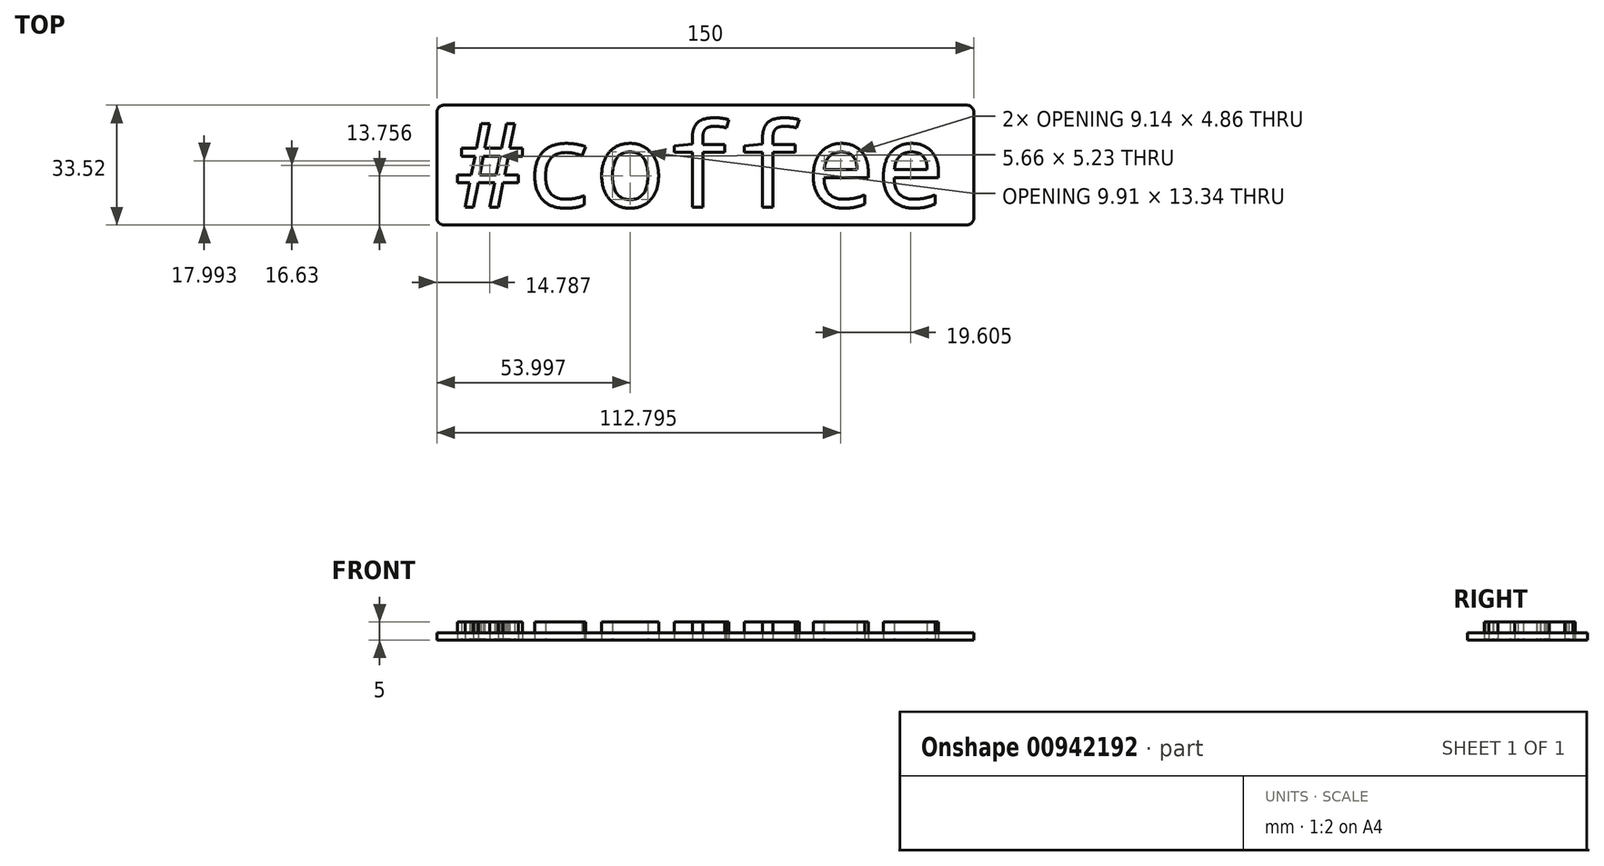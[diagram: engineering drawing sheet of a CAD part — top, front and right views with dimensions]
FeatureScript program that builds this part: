
annotation { "Feature Type Name" : "Feature", "Feature Type Description" : "" }
export const myFeature = defineFeature(function(context is Context, id is Id, definition is map)
    precondition{}
    {
        {
            var Q0;
            Q0=qCreatedBy(makeId("Top.planeOp"),FACE);
            var sketch = newSketch(context, id + "F0", { "sketchPlane" : qUnion([Q0])});
            skText(sketch, "E0", { "text": "#coffee", "fontName": "DroidSansMono.ttf"});
            skLineSegment(sketch, "E1", {"start": v(-62.08, 13.48) * mm, "end": v(-62.08, 18.48) * mm, "construction": true});
            skLineSegment(sketch, "E2", {"start": v(-62.08, -10.04) * mm, "end": v(-62.08, -15.04) * mm, "construction": true});
            const initialGuessF0  = {"E0": [-0.06208, -0.01004, 1, 0, 0.02352]};
            skSetInitialGuess(sketch, initialGuessF0);
            skSolve(sketch);
        }
        {
            var Q0;
            Q0=qCreatedBy(makeId("Top.planeOp"),FACE);
            var sketch = newSketch(context, id + "F1", { "sketchPlane" : qUnion([Q0])});
            skLineSegment(sketch, "E3", {"start": v(-62.08, 13.48) * mm, "end": v(-62.08, 18.48) * mm, "construction": true});
            skLineSegment(sketch, "E4", {"start": v(-62.08, 18.48) * mm, "end": v(-67.08, 18.48) * mm, "construction": true});
            skLineSegment(sketch, "E5", {"start": v(-62.08, -10.04) * mm, "end": v(-62.08, -15.04) * mm, "construction": true});
            skLineSegment(sketch, "E6", {"start": v(-62.08, -15.04) * mm, "end": v(-67.08, -15.04) * mm, "construction": true});
            skLineSegment(sketch, "E7", {"start": v(77.92, -10.04) * mm, "end": v(77.92, -15.04) * mm, "construction": true});
            skLineSegment(sketch, "E8", {"start": v(77.92, -15.04) * mm, "end": v(82.92, -15.04) * mm, "construction": true});
            skLineSegment(sketch, "E9.bottom", {"start": v(-65.08, 18.48) * mm, "end": v(80.92, 18.48) * mm});
            skLineSegment(sketch, "E9.top", {"start": v(-65.08, -15.04) * mm, "end": v(80.92, -15.04) * mm});
            skLineSegment(sketch, "E9.left", {"start": v(-67.08, 16.48) * mm, "end": v(-67.08, -13.04) * mm});
            skLineSegment(sketch, "E9.right", {"start": v(82.92, 16.48) * mm, "end": v(82.92, -13.04) * mm});
            skPoint(sketch, "E10.visualSharp", {"position": v(82.92, 18.48) * mm});
            skArc(sketch, "E10.filletArc", {"start": v(82.92, 16.48) * mm, "mid": v(82.33, 17.9) * mm, "end": v(80.92, 18.48) * mm});
            skPoint(sketch, "E11.visualSharp", {"position": v(82.92, -15.04) * mm});
            skArc(sketch, "E11.filletArc", {"start": v(80.92, -15.04) * mm, "mid": v(82.33, -14.45) * mm, "end": v(82.92, -13.04) * mm});
            skPoint(sketch, "E12.visualSharp", {"position": v(-67.08, 18.48) * mm});
            skArc(sketch, "E12.filletArc", {"start": v(-65.08, 18.48) * mm, "mid": v(-66.5, 17.9) * mm, "end": v(-67.08, 16.48) * mm});
            skPoint(sketch, "E13.visualSharp", {"position": v(-67.08, -15.04) * mm});
            skArc(sketch, "E13.filletArc", {"start": v(-67.08, -13.04) * mm, "mid": v(-66.5, -14.45) * mm, "end": v(-65.08, -15.04) * mm});
            skSolve(sketch);
        }
        {
            var Q0;
            Q0=makeQuery(id+"F1.imprint","IMPRINT",FACE,{"disambiguationData":[TD([[makeQuery(id+"F1.imprint","IMPRINT",EDGE,{"derivedFrom":sQuery(id+"F1.wireOp",EDGE,"E9.bottom")}),-1.0]])]});
            extrude(context, id + "F2", {"entities" : qUnion([Q0]), "depth" : 2 * mm, "offsetDistance" : 25 * mm});
        }
        {
            var Q0;
            Q0 = qSketchRegion(id + "F0", true);
            var Q1;
            Q1 = qConstructionFilter(qBodyType(qCreatedBy(id + "F0" ,EDGE), BodyType.WIRE), ConstructionObject.NO);
            extrude(context, id + "F3", {"entities" : qUnion([Q0]), "surfaceEntities" : qUnion([Q1]), "depth" : 5 * mm, "offsetDistance" : 25 * mm});
        }
    });
